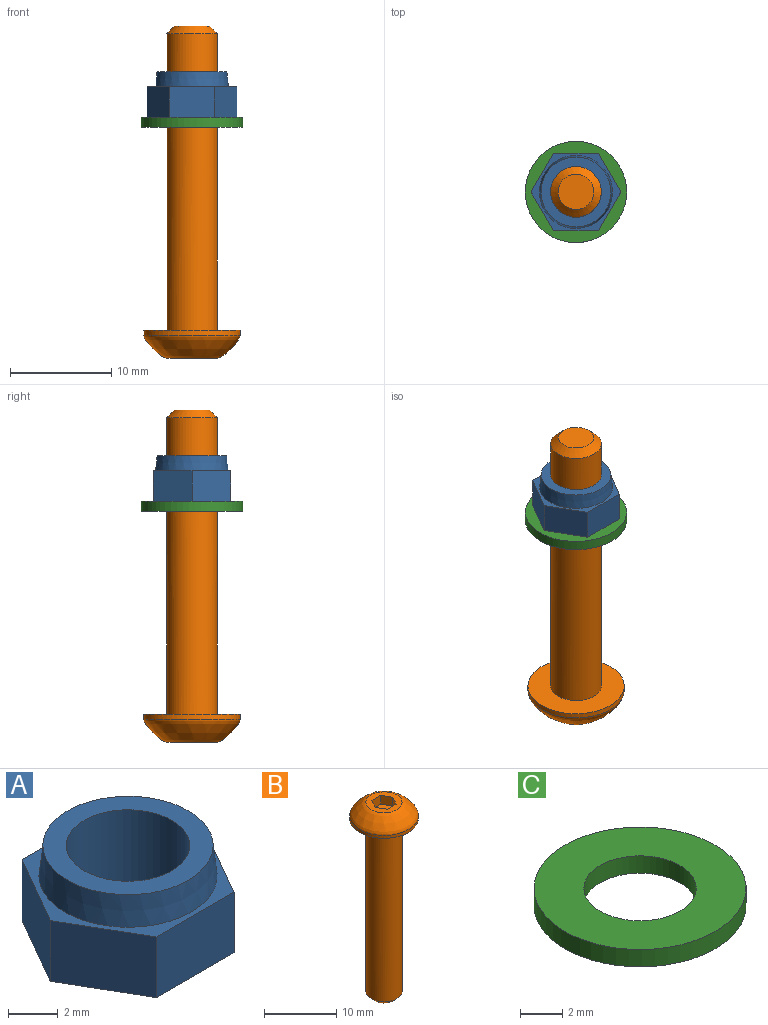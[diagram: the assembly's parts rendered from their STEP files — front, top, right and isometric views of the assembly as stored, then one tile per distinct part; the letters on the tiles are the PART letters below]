
ASSEMBLY  parts=3 mates=1
PART A: 11 faces, bbox 8.9x7.7x4.5 mm
  f0: plane 3.84x3mm, normal (-0.87,0.5,0), area 13.3mm2, adj f1,f5,f6,f7
  f1: plane 3.84x3mm, normal (-0.87,-0.5,0), area 13.3mm2, adj f0,f2,f6,f7
  f2: plane 4.43x3mm, normal (0,-1,0), area 13.3mm2, adj f1,f3,f6,f7
  f3: plane 3.84x3mm, normal (0.87,-0.5,0), area 13.3mm2, adj f2,f4,f6,f7
  f4: plane 3.84x3mm, normal (0.87,0.5,0), area 13.3mm2, adj f3,f5,f6,f7
  f5: plane 4.43x3mm, normal (0,1,0), area 13.3mm2, adj f0,f4,f6,f7
  f6: plane 8.87x7.68mm, normal (0,0,1), area 10.4mm2, adj f0,f1,f2,f3,f4,f5,f8
  f7: plane 8.87x7.68mm, normal (0,0,-1), area 31.4mm2, adj f0,f1,f2,f3,f4,f5,f10
  f8: cone r=3.6mm half-angle=6deg, axis (0,0,-1), area 33.4mm2, adj f6,f9
  f9: plane 6.88x6.88mm, normal (0,0,1), area 17.6mm2, adj f8,f10
  f10: cylinder r=2.5mm len=5mm, axis (0,0,1), area 70.7mm2, adj f7,f9
PART B: 14 faces, bbox 9.5x9.5x32.8 mm
  f0: plane 5.01x5.01mm, normal (0,0,1), area 11.8mm2, adj f3,f4,f5,f6,f7,f8,f10
  f1: cylinder r=4.75mm len=9.5mm, axis (0,0,-1), area 14.9mm2, adj f2,f10
  f2: plane 9.5x9.5mm, normal (0,0,-1), area 51.2mm2, adj f1,f11
  f3: plane 1.5x1.5mm, normal (-0.87,-0.5,0), area 2.6mm2, adj f0,f4,f8,f9
  f4: plane 1.73x1.5mm, normal (0,-1,0), area 2.6mm2, adj f0,f3,f5,f9
  f5: plane 1.5x1.5mm, normal (0.87,-0.5,0), area 2.6mm2, adj f0,f4,f6,f9
  f6: plane 1.5x1.5mm, normal (0.87,0.5,0), area 2.6mm2, adj f0,f5,f7,f9
  f7: plane 1.73x1.5mm, normal (0,1,0), area 2.6mm2, adj f0,f6,f8,f9
  f8: plane 1.5x1.5mm, normal (-0.87,0.5,0), area 2.6mm2, adj f0,f3,f7,f9
  f9: plane 3.46x3mm, normal (0,0,1), area 7.8mm2, adj f3,f4,f5,f6,f7,f8
  f10: bspline ~9.5x9.5mm, area 78.3mm2, adj f0,f1
  f11: cylinder r=2.5mm len=29.25mm, axis (0,0,1), area 459.5mm2, adj f2,f13
  f12: plane 3.5x3.5mm, normal (0,0,-1), area 9.6mm2, adj f13
  f13: cone r=1.75mm half-angle=45deg, axis (0,0,1), area 14.2mm2, adj f11,f12
PART C: 4 faces, bbox 10x10x1 mm
  f0: cylinder r=2.65mm len=5.3mm, axis (0,0,-1), area 16.7mm2, adj f2,f3
  f1: cylinder r=5mm len=10mm, axis (0,0,-1), area 31.4mm2, adj f2,f3
  f2: plane 10x10mm, normal (0,0,1), area 56.5mm2, adj f0,f1
  f3: plane 10x10mm, normal (0,0,-1), area 56.5mm2, adj f0,f1
PLACE A t=(-13.81,-6.82,11.96)mm
PLACE B rot(axis=(1,0,0),180deg) t=(48.69,-6.82,-9.04)mm
PLACE C t=(-13.81,-6.82,10.96)mm
MATE fastened C.f0 <-> A.f8  axis (0,0,1) through (-13.81,-6.82,11.96)mm
